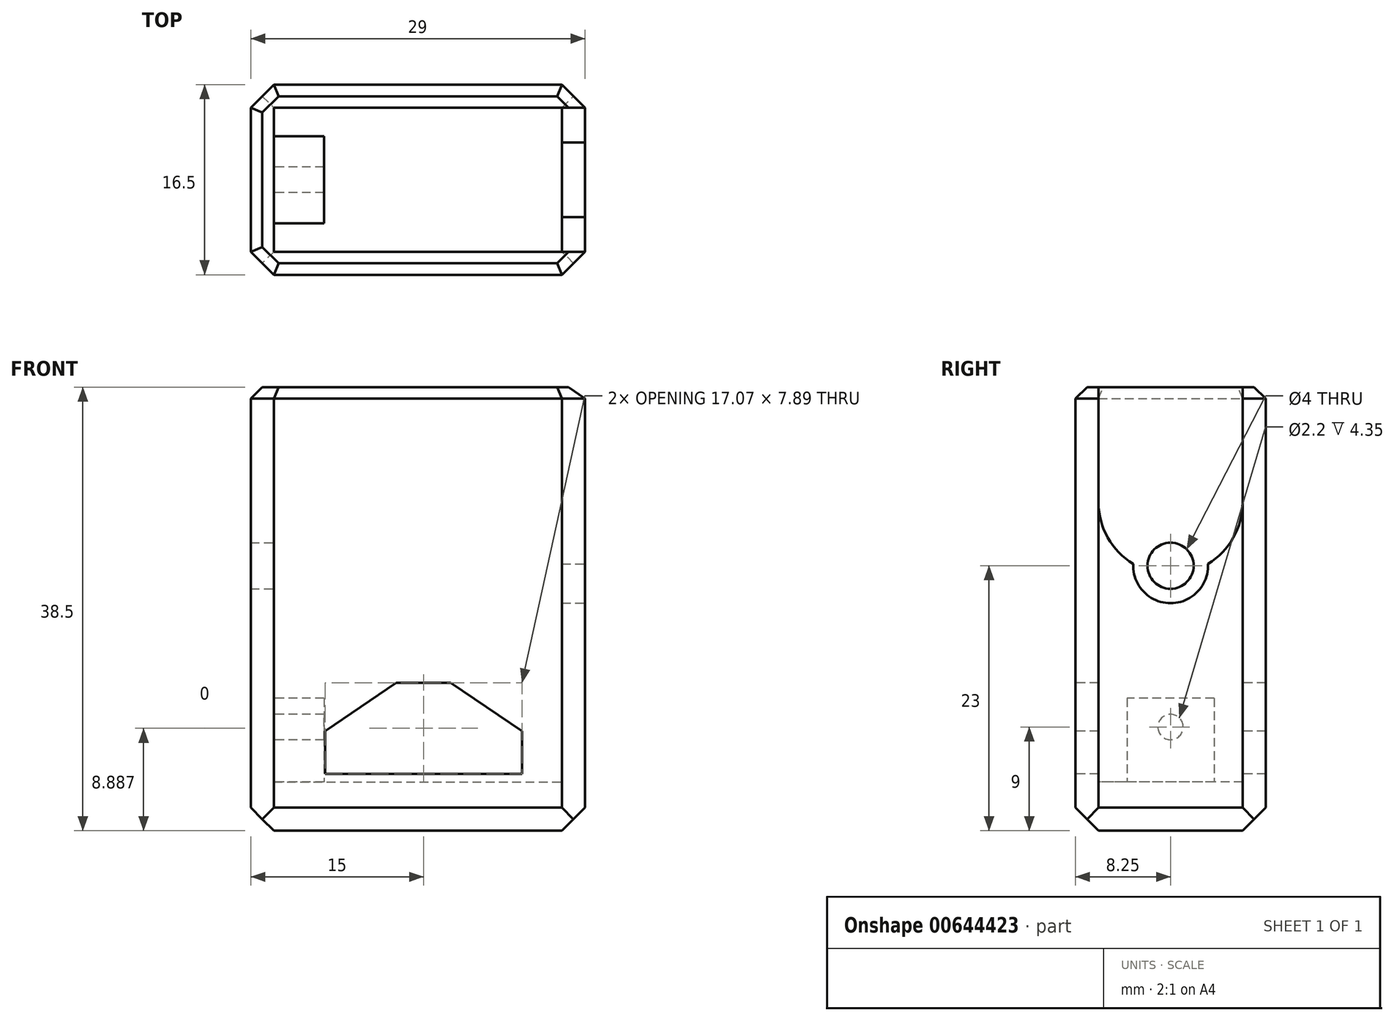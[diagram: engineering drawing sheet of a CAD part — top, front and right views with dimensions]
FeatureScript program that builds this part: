
annotation { "Feature Type Name" : "Feature", "Feature Type Description" : "" }
export const myFeature = defineFeature(function(context is Context, id is Id, definition is map)
    precondition{}
    {
        {
            var Q0;
            Q0=qCreatedBy(makeId("Top.planeOp"),FACE);
            var sketch = newSketch(context, id + "F0", { "sketchPlane" : qUnion([Q0])});
            skLineSegment(sketch, "E0.bottom", {"start": v(0, 16.5) * mm, "end": v(29, 16.5) * mm});
            skLineSegment(sketch, "E0.top", {"start": v(0, 0) * mm, "end": v(29, 0) * mm});
            skLineSegment(sketch, "E0.left", {"start": v(0, 16.5) * mm, "end": v(0, 0) * mm});
            skLineSegment(sketch, "E0.right", {"start": v(29, 16.5) * mm, "end": v(29, 0) * mm});
            skSolve(sketch);
        }
        {
            var Q0;
            Q0 = qSketchRegion(id + "F0", true);
            extrude(context, id + "F1", {"entities" : qUnion([Q0]), "depth" : 38.5 * mm, "offsetDistance" : 25 * mm});
        }
        {
            var Q0;
            Q0=makeQuery(id+"F1.opExtrude","CAP_FACE",FACE,{"disambiguationData":[OSD([sQuery(id+"F0.wireOp",EDGE,"E0.bottom"),sQuery(id+"F0.wireOp",EDGE,"E0.top"),sQuery(id+"F0.wireOp",EDGE,"E0.left"),sQuery(id+"F0.wireOp",EDGE,"E0.right")])],"isStart":false});
            shell(context, id + "F2", {"entities" : qUnion([Q0]), "thickness" : 2 * mm});
        }
        {
            var Q0;
            Q0=makeQuery(id+"F2.opShell","OFFSET_FACE",FACE,{"disambiguationData":[OSD([sQuery(id+"F0.wireOp",EDGE,"E0.bottom"),sQuery(id+"F0.wireOp",EDGE,"E0.top"),sQuery(id+"F0.wireOp",EDGE,"E0.left"),sQuery(id+"F0.wireOp",EDGE,"E0.right")])]});
            extrude(context, id + "F3", {"entities" : qUnion([Q0]), "operationType" : NewBodyOperationType.ADD, "depth" : 2.25 * mm, "offsetDistance" : 25 * mm});
        }
        {
            var Q0;
            Q0=makeQuery(id+"F1.opExtrude","SWEPT_EDGE",EDGE,{"disambiguationData":[OSD([sQuery(id+"F0.wireOp",EDGE,"E0.top"),sQuery(id+"F0.wireOp",EDGE,"E0.right")])]});
            var Q1;
            Q1=makeQuery(id+"F1.opExtrude","SWEPT_EDGE",EDGE,{"disambiguationData":[OSD([sQuery(id+"F0.wireOp",EDGE,"E0.bottom"),sQuery(id+"F0.wireOp",EDGE,"E0.right")])]});
            var Q2;
            Q2=makeQuery(id+"F1.opExtrude","SWEPT_EDGE",EDGE,{"disambiguationData":[OSD([sQuery(id+"F0.wireOp",EDGE,"E0.bottom"),sQuery(id+"F0.wireOp",EDGE,"E0.left")])]});
            var Q3;
            Q3=makeQuery(id+"F1.opExtrude","SWEPT_EDGE",EDGE,{"disambiguationData":[OSD([sQuery(id+"F0.wireOp",EDGE,"E0.top"),sQuery(id+"F0.wireOp",EDGE,"E0.left")])]});
            chamfer(context, id + "F4", {"entities" : qUnion([Q0, Q1, Q2, Q3]), "width" : 2 * mm, "tangentPropagation" : true});
        }
        {
            var Q0;
            Q0=makeQuery(id+"F1.opExtrude","CAP_EDGE",EDGE,{"disambiguationData":[OSD([sQuery(id+"F0.wireOp",EDGE,"E0.top")])],"isStart":true});
            var Q1;
            Q1=makeQuery(id+"F1.opExtrude","CAP_EDGE",EDGE,{"disambiguationData":[OSD([sQuery(id+"F0.wireOp",EDGE,"E0.right")])],"isStart":true});
            var Q2;
            Q2=makeQuery(id+"F1.opExtrude","CAP_EDGE",EDGE,{"disambiguationData":[OSD([sQuery(id+"F0.wireOp",EDGE,"E0.left")])],"isStart":true});
            var Q3;
            Q3=makeQuery(id+"F1.opExtrude","CAP_EDGE",EDGE,{"disambiguationData":[OSD([sQuery(id+"F0.wireOp",EDGE,"E0.bottom")])],"isStart":true});
            chamfer(context, id + "F5", {"entities" : qUnion([Q0, Q1, Q2, Q3]), "width" : 2 * mm, "tangentPropagation" : true});
        }
        {
            var Q0;
            Q0=makeQuery(id+"F1.opExtrude","CAP_EDGE",EDGE,{"disambiguationData":[OSD([sQuery(id+"F0.wireOp",EDGE,"E0.right")])],"isStart":false});
            var Q1;
            {var subQ0=sQuery(id+"F0.wireOp",EDGE,"E0.right");var subQ1=sQuery(id+"F0.wireOp",EDGE,"E0.bottom");Q1=makeQuery(id+"F4.opChamfer","BLEND_EDGE",EDGE,{"blendedFrom":[makeQuery(id+"F1.opExtrude","SWEPT_EDGE",EDGE,{"disambiguationData":[OSD([subQ1,subQ0])]}),makeQuery(id+"F1.opExtrude","CAP_FACE",FACE,{"disambiguationData":[OSD([subQ1,sQuery(id+"F0.wireOp",EDGE,"E0.top"),sQuery(id+"F0.wireOp",EDGE,"E0.left"),subQ0])],"isStart":false})],"blendedInto":[makeQuery(id+"F1.opExtrude","CAP_FACE",FACE,{"disambiguationData":[OSD([subQ1,sQuery(id+"F0.wireOp",EDGE,"E0.top"),sQuery(id+"F0.wireOp",EDGE,"E0.left"),subQ0])],"isStart":false})]});}
            var Q2;
            Q2=makeQuery(id+"F1.opExtrude","CAP_EDGE",EDGE,{"disambiguationData":[OSD([sQuery(id+"F0.wireOp",EDGE,"E0.bottom")])],"isStart":false});
            var Q3;
            {var subQ0=sQuery(id+"F0.wireOp",EDGE,"E0.left");var subQ1=sQuery(id+"F0.wireOp",EDGE,"E0.bottom");Q3=makeQuery(id+"F4.opChamfer","BLEND_EDGE",EDGE,{"blendedFrom":[makeQuery(id+"F1.opExtrude","SWEPT_EDGE",EDGE,{"disambiguationData":[OSD([subQ1,subQ0])]}),makeQuery(id+"F1.opExtrude","CAP_FACE",FACE,{"disambiguationData":[OSD([subQ1,sQuery(id+"F0.wireOp",EDGE,"E0.top"),subQ0,sQuery(id+"F0.wireOp",EDGE,"E0.right")])],"isStart":false})],"blendedInto":[makeQuery(id+"F1.opExtrude","CAP_FACE",FACE,{"disambiguationData":[OSD([subQ1,sQuery(id+"F0.wireOp",EDGE,"E0.top"),subQ0,sQuery(id+"F0.wireOp",EDGE,"E0.right")])],"isStart":false})]});}
            var Q4;
            Q4=makeQuery(id+"F1.opExtrude","CAP_EDGE",EDGE,{"disambiguationData":[OSD([sQuery(id+"F0.wireOp",EDGE,"E0.left")])],"isStart":false});
            var Q5;
            {var subQ0=sQuery(id+"F0.wireOp",EDGE,"E0.left");var subQ1=sQuery(id+"F0.wireOp",EDGE,"E0.top");Q5=makeQuery(id+"F4.opChamfer","BLEND_EDGE",EDGE,{"blendedFrom":[makeQuery(id+"F1.opExtrude","SWEPT_EDGE",EDGE,{"disambiguationData":[OSD([subQ1,subQ0])]}),makeQuery(id+"F1.opExtrude","CAP_FACE",FACE,{"disambiguationData":[OSD([sQuery(id+"F0.wireOp",EDGE,"E0.bottom"),subQ1,subQ0,sQuery(id+"F0.wireOp",EDGE,"E0.right")])],"isStart":false})],"blendedInto":[makeQuery(id+"F1.opExtrude","CAP_FACE",FACE,{"disambiguationData":[OSD([sQuery(id+"F0.wireOp",EDGE,"E0.bottom"),subQ1,subQ0,sQuery(id+"F0.wireOp",EDGE,"E0.right")])],"isStart":false})]});}
            var Q6;
            Q6=makeQuery(id+"F1.opExtrude","CAP_EDGE",EDGE,{"disambiguationData":[OSD([sQuery(id+"F0.wireOp",EDGE,"E0.top")])],"isStart":false});
            var Q7;
            {var subQ0=sQuery(id+"F0.wireOp",EDGE,"E0.right");var subQ1=sQuery(id+"F0.wireOp",EDGE,"E0.top");Q7=makeQuery(id+"F4.opChamfer","BLEND_EDGE",EDGE,{"blendedFrom":[makeQuery(id+"F1.opExtrude","SWEPT_EDGE",EDGE,{"disambiguationData":[OSD([subQ1,subQ0])]}),makeQuery(id+"F1.opExtrude","CAP_FACE",FACE,{"disambiguationData":[OSD([sQuery(id+"F0.wireOp",EDGE,"E0.bottom"),subQ1,sQuery(id+"F0.wireOp",EDGE,"E0.left"),subQ0])],"isStart":false})],"blendedInto":[makeQuery(id+"F1.opExtrude","CAP_FACE",FACE,{"disambiguationData":[OSD([sQuery(id+"F0.wireOp",EDGE,"E0.bottom"),subQ1,sQuery(id+"F0.wireOp",EDGE,"E0.left"),subQ0])],"isStart":false})]});}
            chamfer(context, id + "F6", {"entities" : qUnion([Q0, Q1, Q2, Q3, Q4, Q5, Q6, Q7]), "width" : 1 * mm, "tangentPropagation" : true});
        }
        {
            var Q0;
            Q0=makeQuery(id+"F1.opExtrude","SWEPT_FACE",FACE,{"disambiguationData":[OSD([sQuery(id+"F0.wireOp",EDGE,"E0.top")])]});
            var sketch = newSketch(context, id + "F7", { "sketchPlane" : qUnion([Q0])});
            skLineSegment(sketch, "E1", {"start": v(6.46, 4.94) * mm, "end": v(23.54, 4.94) * mm});
            skLineSegment(sketch, "E2", {"start": v(23.54, 8.66) * mm, "end": v(23.54, 4.94) * mm});
            skLineSegment(sketch, "E3", {"start": v(17.36, 12.83) * mm, "end": v(23.54, 8.66) * mm});
            skLineSegment(sketch, "E4", {"start": v(17.36, 12.83) * mm, "end": v(12.63, 12.83) * mm});
            skLineSegment(sketch, "E5", {"start": v(12.63, 12.83) * mm, "end": v(6.46, 8.66) * mm});
            skLineSegment(sketch, "E6", {"start": v(6.46, 8.66) * mm, "end": v(6.46, 4.94) * mm});
            skSolve(sketch);
        }
        {
            var Q0;
            Q0=makeQuery(id+"F7.imprint","IMPRINT",FACE,{"disambiguationData":[TD([[makeQuery(id+"F7.imprint","IMPRINT",EDGE,{"derivedFrom":sQuery(id+"F7.wireOp",EDGE,"E1")}),1.0]])]});
            extrude(context, id + "F8", {"entities" : qUnion([Q0]), "operationType" : NewBodyOperationType.REMOVE, "endBound" : BoundingType.THROUGH_ALL, "oppositeDirection" : true, "depth" : 25 * mm, "offsetDistance" : 25 * mm});
        }
        {
            var Q0;
            Q0=makeQuery(id+"F1.opExtrude","SWEPT_FACE",FACE,{"disambiguationData":[OSD([sQuery(id+"F0.wireOp",EDGE,"E0.right")])]});
            var sketch = newSketch(context, id + "F9", { "sketchPlane" : qUnion([Q0])});
            skCircle(sketch, "E7", {"center": v(8.25, 23) * mm, "radius": 3.25 * mm});
            skCircle(sketch, "E8", {"center": v(8.25, 28.5) * mm, "radius": 6.25 * mm});
            skLineSegment(sketch, "E9.bottom", {"start": v(2, 38.5) * mm, "end": v(14.5, 38.5) * mm});
            skLineSegment(sketch, "E9.top", {"start": v(2, 28.5) * mm, "end": v(14.5, 28.5) * mm});
            skLineSegment(sketch, "E9.left", {"start": v(2, 38.5) * mm, "end": v(2, 28.5) * mm});
            skLineSegment(sketch, "E9.right", {"start": v(14.5, 38.5) * mm, "end": v(14.5, 28.5) * mm});
            skSolve(sketch);
        }
        {
            var Q0;
            Q0 = qSketchRegion(id + "F9", true);
            extrude(context, id + "F10", {"entities" : qUnion([Q0]), "operationType" : NewBodyOperationType.REMOVE, "endBound" : BoundingType.UP_TO_NEXT, "oppositeDirection" : true, "depth" : 25 * mm, "offsetDistance" : 25 * mm});
        }
        {
            var Q0;
            Q0=makeQuery(id+"F2.opShell","OFFSET_FACE",FACE,{"disambiguationData":[OSD([sQuery(id+"F0.wireOp",EDGE,"E0.left")])]});
            var sketch = newSketch(context, id + "F11", { "sketchPlane" : qUnion([Q0])});
            skCircle(sketch, "E10", {"center": v(8.25, 23) * mm, "radius": 2 * mm});
            skSolve(sketch);
        }
        {
            var Q0;
            Q0=makeQuery(id+"F11.imprint","IMPRINT",FACE,{"disambiguationData":[TD([[makeQuery(id+"F11.imprint","IMPRINT",EDGE,{"derivedFrom":sQuery(id+"F11.wireOp",EDGE,"E10")}),1.0]])]});
            extrude(context, id + "F12", {"entities" : qUnion([Q0]), "operationType" : NewBodyOperationType.REMOVE, "endBound" : BoundingType.THROUGH_ALL, "oppositeDirection" : true, "depth" : 25 * mm, "offsetDistance" : 25 * mm});
        }
        {
            var Q0;
            Q0=makeQuery(id+"F2.opShell","OFFSET_FACE",FACE,{"disambiguationData":[OSD([sQuery(id+"F0.wireOp",EDGE,"E0.left")])]});
            var sketch = newSketch(context, id + "F13", { "sketchPlane" : qUnion([Q0])});
            skLineSegment(sketch, "E11.bottom", {"start": v(12.02, 11.5) * mm, "end": v(4.48, 11.5) * mm});
            skLineSegment(sketch, "E11.top", {"start": v(12.02, 4.25) * mm, "end": v(4.48, 4.25) * mm});
            skLineSegment(sketch, "E11.left", {"start": v(12.02, 11.5) * mm, "end": v(12.02, 4.25) * mm});
            skLineSegment(sketch, "E11.right", {"start": v(4.48, 11.5) * mm, "end": v(4.48, 4.25) * mm});
            skCircle(sketch, "E12", {"center": v(8.25, 9) * mm, "radius": 1.1 * mm});
            skSolve(sketch);
        }
        {
            var Q0;
            Q0 = qSketchRegion(id + "F13", true);
            extrude(context, id + "F14", {"entities" : qUnion([Q0]), "operationType" : NewBodyOperationType.ADD, "depth" : 4.35 * mm, "offsetDistance" : 25 * mm});
        }
    });
